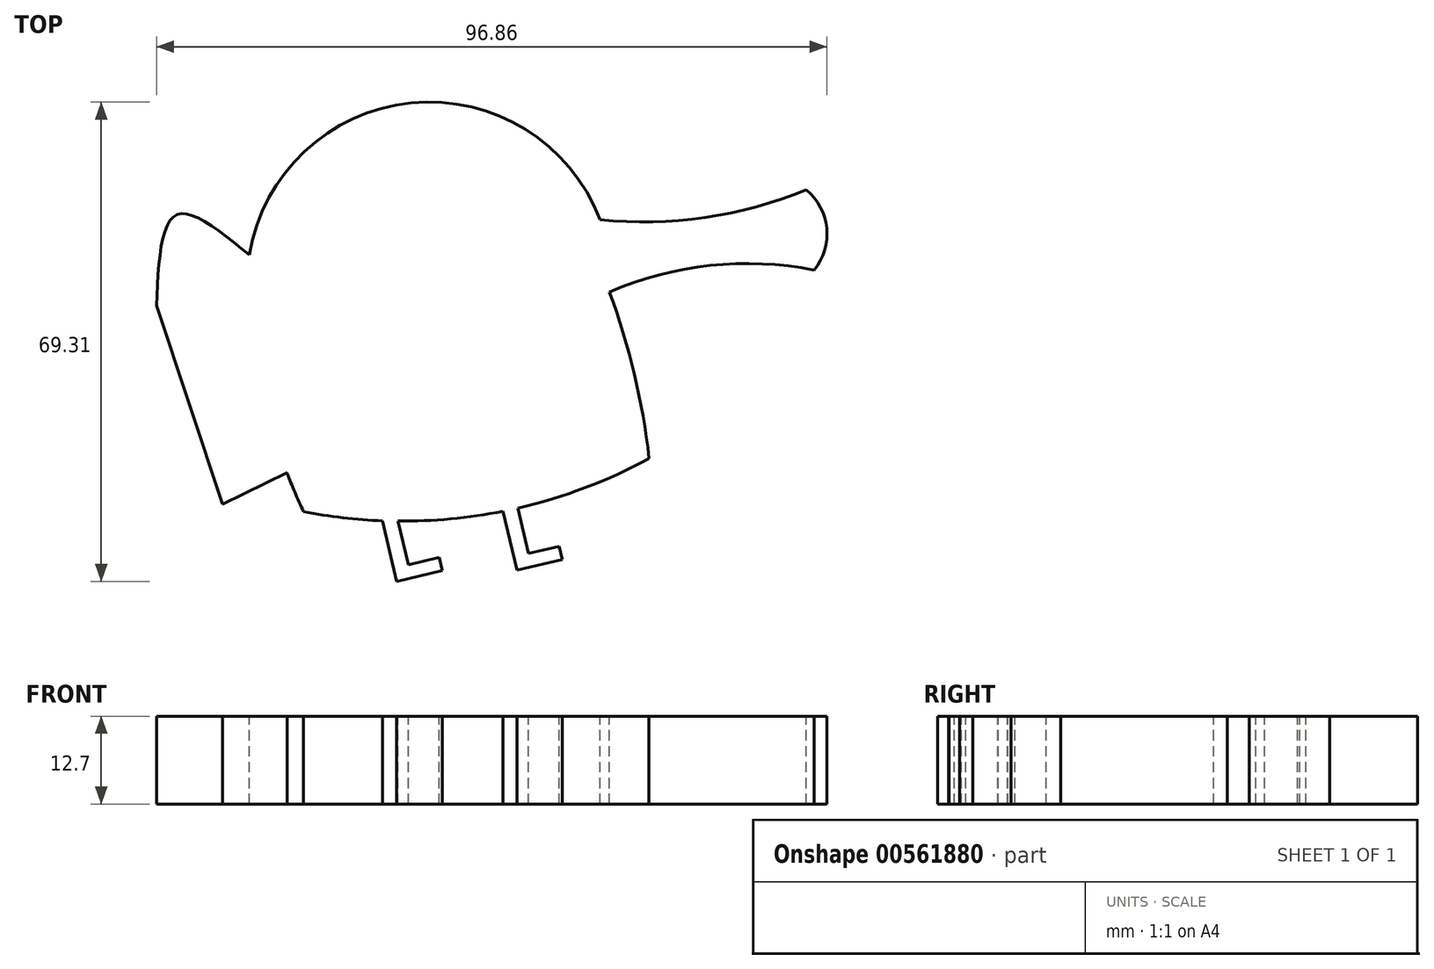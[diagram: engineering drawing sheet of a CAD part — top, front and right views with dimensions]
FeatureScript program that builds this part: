
annotation { "Feature Type Name" : "Feature", "Feature Type Description" : "" }
export const myFeature = defineFeature(function(context is Context, id is Id, definition is map)
    precondition{}
    {
        {
            var Q0;
            Q0=qCreatedBy(makeId("Top.planeOp"),FACE);
            var sketch = newSketch(context, id + "F0", { "sketchPlane" : qUnion([Q0])});
            skLineSegment(sketch, "E0.bottom", {"start": v(-68.77, 59.72) * mm, "end": v(58.23, 59.72) * mm});
            skLineSegment(sketch, "E0.top", {"start": v(-68.77, -67.28) * mm, "end": v(58.23, -67.28) * mm});
            skLineSegment(sketch, "E0.left", {"start": v(-68.77, 59.72) * mm, "end": v(-68.77, -67.28) * mm});
            skLineSegment(sketch, "E0.right", {"start": v(58.23, 59.72) * mm, "end": v(58.23, -67.28) * mm});
            skSolve(sketch);
        }
        {
            var Q0;
            Q0=makeQuery(id+"F0.imprint","IMPRINT",FACE,{"disambiguationData":[TD([[makeQuery(id+"F0.imprint","IMPRINT",EDGE,{"derivedFrom":sQuery(id+"F0.wireOp",EDGE,"E0.bottom")}),-1.0]])]});
            extrude(context, id + "F1", {"entities" : qUnion([Q0]), "depth" : 12.7 * mm, "offsetDistance" : 25.4 * mm});
        }
        {
            var Q0;
            Q0=makeQuery(id+"F1.opExtrude","CAP_FACE",FACE,{"disambiguationData":[OSD([sQuery(id+"F0.wireOp",EDGE,"E0.bottom"),sQuery(id+"F0.wireOp",EDGE,"E0.top"),sQuery(id+"F0.wireOp",EDGE,"E0.left"),sQuery(id+"F0.wireOp",EDGE,"E0.right")])],"isStart":false});
            var sketch = newSketch(context, id + "F2", { "sketchPlane" : qUnion([Q0])});
            skArc(sketch, "E1", {"start": v(5.6, 23.64) * mm, "mid": v(-21.68, 40.51) * mm, "end": v(-45.06, 18.55) * mm});
            skArc(sketch, "E2", {"start": v(5.6, 23.64) * mm, "mid": v(20.76, 23.95) * mm, "end": v(35.4, 27.96) * mm});
            skArc(sketch, "E3", {"start": v(-45.06, 18.55) * mm, "mid": v(-43.33, -0.48) * mm, "end": v(-37.22, -18.58) * mm});
            skArc(sketch, "E4", {"start": v(-37.22, -18.58) * mm, "mid": v(-11.6, -19.09) * mm, "end": v(12.7, -10.9) * mm});
            skArc(sketch, "E5", {"start": v(12.7, -10.9) * mm, "mid": v(10.56, 1.31) * mm, "end": v(6.96, 13.17) * mm});
            skLineSegment(sketch, "E6", {"start": v(-25.82, -19.9) * mm, "end": v(-23.76, -28.67) * mm});
            skLineSegment(sketch, "E7", {"start": v(-23.76, -28.67) * mm, "end": v(-17.17, -27.12) * mm});
            skLineSegment(sketch, "E8", {"start": v(-17.17, -27.12) * mm, "end": v(-17.62, -25.22) * mm});
            skLineSegment(sketch, "E9", {"start": v(-17.62, -25.22) * mm, "end": v(-22.1, -26.28) * mm});
            skLineSegment(sketch, "E10", {"start": v(-22.1, -26.28) * mm, "end": v(-23.58, -19.95) * mm});
            skLineSegment(sketch, "E11", {"start": v(-17, -19.72) * mm, "end": v(-15, -28.27) * mm});
            skLineSegment(sketch, "E12", {"start": v(-15, -28.27) * mm, "end": v(-8.4, -26.73) * mm});
            skLineSegment(sketch, "E13", {"start": v(-8.4, -26.73) * mm, "end": v(-8.85, -24.83) * mm});
            skLineSegment(sketch, "E14", {"start": v(-8.85, -24.83) * mm, "end": v(-13.47, -25.91) * mm});
            skLineSegment(sketch, "E15", {"start": v(-13.47, -25.91) * mm, "end": v(-14.96, -19.54) * mm});
            skLineSegment(sketch, "E16", {"start": v(-8.4, -18.52) * mm, "end": v(-6.4, -27.05) * mm});
            skLineSegment(sketch, "E17", {"start": v(-6.4, -27.05) * mm, "end": v(0.16, -25.5) * mm});
            skLineSegment(sketch, "E18", {"start": v(0.16, -25.5) * mm, "end": v(-0.28, -23.6) * mm});
            skLineSegment(sketch, "E19", {"start": v(-0.28, -23.6) * mm, "end": v(-4.7, -24.64) * mm});
            skLineSegment(sketch, "E20", {"start": v(-4.7, -24.64) * mm, "end": v(-6.25, -18.06) * mm});
            skLineSegment(sketch, "E21", {"start": v(0, -16.34) * mm, "end": v(1.85, -24.2) * mm});
            skLineSegment(sketch, "E22", {"start": v(1.85, -24.2) * mm, "end": v(8.66, -22.6) * mm});
            skLineSegment(sketch, "E23", {"start": v(8.66, -22.6) * mm, "end": v(8.21, -20.7) * mm});
            skLineSegment(sketch, "E24", {"start": v(8.21, -20.7) * mm, "end": v(3.33, -21.86) * mm});
            skLineSegment(sketch, "E25", {"start": v(3.33, -21.86) * mm, "end": v(1.88, -15.7) * mm});
            skLineSegment(sketch, "E26", {"start": v(-39.63, -12.97) * mm, "end": v(-48.91, -17.49) * mm});
            skLineSegment(sketch, "E27", {"start": v(-48.91, -17.49) * mm, "end": v(-58.47, 11.18) * mm});
            skFitSpline(sketch, "E28", {"points": [v(-58.47, 11.18) * mm, v(-55.59, 24.33) * mm, v(-45.06, 18.55) * mm], "startDerivative": vector(1.36, 35.47) * mm, "endDerivative": vector(26.82, -21.25) * mm});
            skArc(sketch, "E29", {"start": v(36.53, 16.37) * mm, "mid": v(21.5, 17) * mm, "end": v(6.96, 13.17) * mm});
            skArc(sketch, "E30", {"start": v(36.53, 16.37) * mm, "mid": v(38.35, 22.4) * mm, "end": v(35.4, 27.96) * mm});
            skSolve(sketch);
        }
        {
            var Q0;
            Q0=makeQuery(id+"F2.imprint","IMPRINT",FACE,{"disambiguationData":[TD([[makeQuery(id+"F2.imprint","IMPRINT",EDGE,{"derivedFrom":sQuery(id+"F2.wireOp",EDGE,"E1")}),-1.0]])]});
            extrude(context, id + "F3", {"entities" : qUnion([Q0]), "operationType" : NewBodyOperationType.REMOVE, "oppositeDirection" : true, "depth" : 25.4 * mm, "offsetDistance" : 25.4 * mm});
        }
    });
